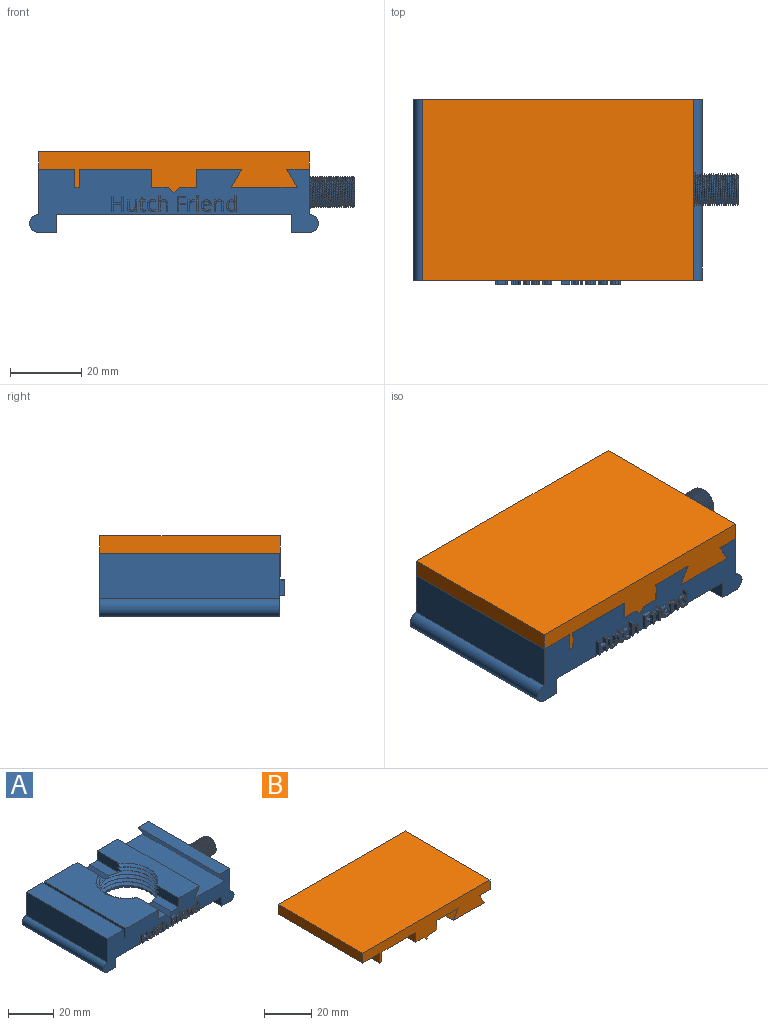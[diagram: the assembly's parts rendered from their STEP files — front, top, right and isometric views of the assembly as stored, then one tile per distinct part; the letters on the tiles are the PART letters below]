
ASSEMBLY  parts=2 mates=1
PART A: 264 faces, bbox 92x52.4x19.3 mm
  f0: cylinder r=12.7mm len=15.02mm, axis (0,0,-1), area 1.5mm2, adj f18,f23,f257,f259
  f1: cylinder r=12.7mm len=22mm, axis (0,0,-1), area 2.7mm2, adj f19,f22,f260,f262
  f2: cylinder r=12.7mm len=22mm, axis (0,0,-1), area 2.7mm2, adj f20,f23,f255,f258
  f3: cylinder r=12.7mm len=22mm, axis (0,0,-1), area 2.7mm2, adj f19,f22,f254,f261
  f4: cylinder r=12.7mm len=22mm, axis (0,0,-1), area 2.7mm2, adj f20,f23,f251,f256
  f5: cylinder r=12.7mm len=23.65mm, axis (0,0,-1), area 3.2mm2, adj f22,f43,f247,f253
  f6: cylinder r=12.7mm len=25.36mm, axis (0,0,-1), area 3.9mm2, adj f42,f45,f248,f252
  f7: plane 81.28x17.78mm, normal (0,-1,0), area 841.9mm2, adj f11,f12,f13,f14,f15,f16,f17,f18
  f8: cylinder r=12.7mm len=25.4mm, axis (0,0,-1), area 96.4mm2, adj f12,f44,f248,f249,f250
  f9: plane 81.28x17.78mm, normal (0,1,0), area 886.7mm2, adj f10,f12,f13,f14,f15,f16,f17,f18
  f10: plane 13.32x4.81mm, normal (0,0,1), area 59.4mm2, adj f9,f20,f42,f252
  f11: plane 13.21x4.83mm, normal (0,0,1), area 58.9mm2, adj f7,f23,f45,f251
  f12: plane 66.04x50.8mm, normal (0,0,-1), area 2848.1mm2, adj f7,f8,f9,f32,f34
  f13: plane 50.8x6.35mm, normal (0,0,1), area 322.6mm2, adj f7,f9,f16,f30
  f14: plane 51.12x20.64mm, normal (0,0,1), area 894.7mm2, adj f7,f9,f19,f22,f26,f262,f263
  f15: plane 50.8x10.16mm, normal (0,0,1), area 516.1mm2, adj f7,f9,f17,f25
  f16: plane 50.8x12.7mm, normal (1,0,0), area 510.6mm2, adj f7,f9,f13,f31,f36,f38,f40,f238
  f17: plane 50.8x12.7mm, normal (-1,0,0), area 645.2mm2, adj f7,f9,f15,f37
  f18: plane 51.04x12.94mm, normal (0,0,1), area 540.1mm2, adj f0,f7,f9,f20,f23,f28,f257,f259
  f19: plane 14.46x5.14mm, normal (1,0,0), area 68.2mm2, adj f1,f3,f9,f14,f21,f253,f254,f260
  f20: plane 14.46x5.14mm, normal (-1,0,0), area 68.2mm2, adj f2,f4,f9,f10,f18,f251,f252,f255
  f21: plane 14x4.87mm, normal (0,0,1), area 61.1mm2, adj f9,f19,f43,f253
  f22: plane 14.46x5.14mm, normal (1,0,0), area 69.1mm2, adj f1,f3,f5,f7,f14,f24,f247,f253
  f23: plane 14.46x5.14mm, normal (-1,0,0), area 69.1mm2, adj f0,f2,f4,f7,f11,f18,f251,f255
  f24: plane 13.86x4.85mm, normal (0,0,1), area 60.6mm2, adj f7,f22,f44,f247
  f25: plane 50.8x5.08mm, normal (1,0,0), area 258.1mm2, adj f7,f9,f15,f27
  f26: plane 50.8x5.08mm, normal (-1,0,0), area 258.1mm2, adj f7,f9,f14,f27
  f27: plane 50.8x1.27mm, normal (0,0,1), area 64.5mm2, adj f7,f9,f25,f26
  f28: plane 50.8x5.08mm, normal (0.87,0,-0.5), area 298mm2, adj f7,f9,f18,f29
  f29: plane 50.8x18.57mm, normal (0,0,1), area 943.1mm2, adj f7,f9,f28,f30
  f30: plane 50.8x5.08mm, normal (-0.87,0,-0.5), area 298mm2, adj f7,f9,f13,f29
  f31: cylinder r=4.76mm len=9.53mm, axis (-1,0,0), area 7.5mm2, adj f16,f236,f238
  f32: plane 50.8x5.08mm, normal (1,0,0), area 258.1mm2, adj f7,f9,f12,f33
  f33: plane 50.8x5.08mm, normal (0,0,-1), area 258.1mm2, adj f7,f9,f32,f37
  f34: plane 50.8x5.08mm, normal (-1,0,0), area 258.1mm2, adj f7,f9,f12,f35
  f35: plane 50.8x5.08mm, normal (0,0,-1), area 258.1mm2, adj f7,f9,f34,f36
  f36: cylinder r=2.54mm len=50.8mm, axis (0,-1,0), area 405.4mm2, adj f7,f9,f16,f35
  f37: cylinder r=2.54mm len=50.8mm, axis (0,-1,0), area 405.4mm2, adj f7,f9,f17,f33
  f38: cylinder r=3.17mm len=6.35mm, axis (1,0,0), area 50.7mm2, adj f16,f39
  f39: plane 6.35x6.35mm, normal (1,0,0), area 31.7mm2, adj f38
  f40: cylinder r=3.17mm len=6.35mm, axis (1,0,0), area 50.7mm2, adj f16,f41
  f41: plane 6.35x6.35mm, normal (1,0,0), area 31.7mm2, adj f40
  f42: plane 12.81x1.64mm, normal (-0.71,0,0.71), area 27mm2, adj f6,f9,f10,f43,f248,f249,f252
  f43: plane 12.82x1.65mm, normal (0.71,0,0.71), area 27mm2, adj f5,f9,f21,f42,f247,f249,f253
  f44: plane 12.75x1.63mm, normal (0.71,0,0.71), area 26.6mm2, adj f7,f8,f24,f45,f247,f248,f249
  f45: plane 12.75x1.64mm, normal (-0.71,0,0.71), area 26.6mm2, adj f6,f7,f11,f44,f248,f251,f252
  f46: plane 1.3x0.5mm, normal (0,0,-1), area 0.6mm2, adj f7,f47,f57,f58
  f47: plane 4.29x1.3mm, normal (1,0,0), area 5.6mm2, adj f7,f46,f48,f58
  f48: plane 1.3x0.5mm, normal (0,0,1), area 0.6mm2, adj f7,f47,f49,f58
  f49: plane 1.83x1.3mm, normal (-1,0,0), area 2.4mm2, adj f7,f48,f50,f58
  f50: plane 2.26x1.3mm, normal (0,0,1), area 2.9mm2, adj f7,f49,f51,f58
  f51: plane 1.83x1.3mm, normal (1,0,0), area 2.4mm2, adj f7,f50,f52,f58
  f52: plane 1.3x0.5mm, normal (0,0,1), area 0.6mm2, adj f7,f51,f53,f58
  f53: plane 4.29x1.3mm, normal (-1,0,0), area 5.6mm2, adj f7,f52,f54,f58
  f54: plane 1.3x0.5mm, normal (0,0,-1), area 0.6mm2, adj f7,f53,f55,f58
  f55: plane 2.02x1.3mm, normal (1,0,0), area 2.6mm2, adj f7,f54,f56,f58
  f56: plane 2.26x1.3mm, normal (0,0,-1), area 2.9mm2, adj f7,f55,f57,f58
  f57: plane 2.02x1.3mm, normal (-1,0,0), area 2.6mm2, adj f7,f46,f56,f58
  f58: plane 4.29x3.26mm, normal (0,-1,0), area 5.3mm2, adj f46,f47,f48,f49,f50,f51,f52,f53
  f59: plane 2.09x1.3mm, normal (1,0,0), area 2.7mm2, adj f7,f60,f75,f76
  f60: plane 1.3x0.49mm, normal (0,0,1), area 0.6mm2, adj f7,f59,f61,f76
  f61: plane 2.11x1.3mm, normal (-1,0,0), area 2.7mm2, adj f7,f60,f62,f76
  f62: extruded ~1.3x0.89mm, area 1.3mm2, adj f7,f61,f63,f76
  f63: extruded ~1.3x0.88mm, area 1.2mm2, adj f7,f62,f64,f76
  f64: extruded ~1.3x0.61mm, area 0.8mm2, adj f7,f63,f65,f76
  f65: extruded ~1.3x0.42mm, area 0.7mm2, adj f7,f64,f66,f76
  f66: plane 1.3x0.03mm, normal (0,0,-1), area 0mm2, adj f7,f65,f67,f76
  f67: plane 1.3x0.43mm, normal (-0.99,0,-0.16), area 0.6mm2, adj f7,f66,f68,f76
  f68: plane 1.3x0.4mm, normal (0,0,-1), area 0.5mm2, adj f7,f67,f69,f76
  f69: plane 3.22x1.3mm, normal (1,0,0), area 4.2mm2, adj f7,f68,f70,f76
  f70: plane 1.3x0.49mm, normal (0,0,1), area 0.6mm2, adj f7,f69,f71,f76
  f71: plane 1.69x1.3mm, normal (-1,0,0), area 2.2mm2, adj f7,f70,f72,f76
  f72: extruded ~1.3x0.9mm, area 1.2mm2, adj f7,f71,f73,f76
  f73: extruded ~1.3x0.74mm, area 1.1mm2, adj f7,f72,f74,f76
  f74: extruded ~1.3x0.56mm, area 0.8mm2, adj f7,f73,f75,f76
  f75: extruded ~1.3x0.59mm, area 0.8mm2, adj f7,f59,f74,f76
  f76: plane 3.28x2.69mm, normal (0,-1,0), area 3.8mm2, adj f59,f60,f61,f62,f63,f64,f65,f66
  f77: extruded ~1.3x0.25mm, area 0.3mm2, adj f7,f78,f95,f96
  f78: extruded ~1.3x0.38mm, area 0.5mm2, adj f7,f77,f79,f96
  f79: extruded ~1.3x0.45mm, area 0.6mm2, adj f7,f78,f80,f96
  f80: plane 1.89x1.3mm, normal (1,0,0), area 2.5mm2, adj f7,f79,f81,f96
  f81: plane 1.3x0.93mm, normal (0,0,-1), area 1.2mm2, adj f7,f80,f82,f96
  f82: plane 1.3x0.38mm, normal (1,0,0), area 0.5mm2, adj f7,f81,f83,f96
  f83: plane 1.3x0.93mm, normal (0,0,1), area 1.2mm2, adj f7,f82,f84,f96
  f84: plane 1.3x0.75mm, normal (1,0,0), area 1mm2, adj f7,f83,f85,f96
  f85: plane 1.3x0.28mm, normal (0,0,1), area 0.4mm2, adj f7,f84,f86,f96
  f86: plane 1.3x0.69mm, normal (-0.96,0,0.29), area 0.9mm2, adj f7,f85,f87,f96
  f87: plane 1.3x0.46mm, normal (-0.4,0,0.92), area 0.7mm2, adj f7,f86,f88,f96
  f88: plane 1.3x0.24mm, normal (-1,0,0), area 0.3mm2, adj f7,f87,f89,f96
  f89: plane 1.3x0.46mm, normal (0,0,-1), area 0.6mm2, adj f7,f88,f90,f96
  f90: plane 1.92x1.3mm, normal (-1,0,0), area 2.5mm2, adj f7,f89,f91,f96
  f91: extruded ~1.3x0.98mm, area 2mm2, adj f7,f90,f92,f96
  f92: extruded ~1.3x0.28mm, area 0.4mm2, adj f7,f91,f93,f96
  f93: extruded ~1.3x0.23mm, area 0.3mm2, adj f7,f92,f94,f96
  f94: plane 1.3x0.37mm, normal (1,0,0), area 0.5mm2, adj f7,f93,f95,f96
  f95: extruded ~1.3x0.19mm, area 0.3mm2, adj f7,f77,f94,f96
  f96: plane 4.02x1.91mm, normal (0,-1,0), area 2.7mm2, adj f77,f78,f79,f80,f81,f82,f83,f84
  f97: extruded ~1.3x1.08mm, area 1.6mm2, adj f7,f98,f111,f112
  f98: extruded ~1.3x0.81mm, area 1.1mm2, adj f7,f97,f99,f112
  f99: plane 1.3x0.43mm, normal (1,0,0), area 0.6mm2, adj f7,f98,f100,f112
  f100: extruded ~1.3x0.83mm, area 1.1mm2, adj f7,f99,f101,f112
  f101: extruded ~1.3x0.71mm, area 1mm2, adj f7,f100,f102,f112
  f102: extruded ~1.3x0.91mm, area 1.2mm2, adj f7,f101,f103,f112
  f103: extruded ~1.3x1.25mm, area 2.4mm2, adj f7,f102,f104,f112
  f104: extruded ~1.3x0.34mm, area 0.4mm2, adj f7,f103,f105,f112
  f105: extruded ~1.3x0.35mm, area 0.5mm2, adj f7,f104,f106,f112
  f106: plane 1.3x0.41mm, normal (0.94,0,-0.34), area 0.6mm2, adj f7,f105,f107,f112
  f107: extruded ~1.3x0.36mm, area 0.5mm2, adj f7,f106,f108,f112
  f108: extruded ~1.3x0.46mm, area 0.6mm2, adj f7,f107,f109,f112
  f109: extruded ~1.3x1.11mm, area 1.6mm2, adj f7,f108,f110,f112
  f110: extruded ~1.3x1.25mm, area 1.7mm2, adj f7,f109,f111,f112
  f111: extruded ~1.3x1.22mm, area 1.7mm2, adj f7,f97,f110,f112
  f112: plane 3.34x2.33mm, normal (0,-1,0), area 2.7mm2, adj f97,f98,f99,f100,f101,f102,f103,f104
  f113: plane 2.08x1.3mm, normal (-1,0,0), area 2.7mm2, adj f7,f114,f130,f131
  f114: plane 1.3x0.49mm, normal (0,0,-1), area 0.6mm2, adj f7,f113,f115,f131
  f115: plane 2.1x1.3mm, normal (1,0,0), area 2.7mm2, adj f7,f114,f116,f131
  f116: extruded ~1.3x0.89mm, area 1.3mm2, adj f7,f115,f117,f131
  f117: extruded ~1.3x0.89mm, area 1.2mm2, adj f7,f116,f118,f131
  f118: extruded ~1.3x0.61mm, area 0.8mm2, adj f7,f117,f119,f131
  f119: extruded ~1.3x0.41mm, area 0.7mm2, adj f7,f118,f120,f131
  f120: plane 1.3x0.03mm, normal (0,0,1), area 0mm2, adj f7,f119,f121,f131
  f121: extruded ~1.3x0.41mm, area 0.5mm2, adj f7,f120,f122,f131
  f122: plane 1.38x1.3mm, normal (1,0,0), area 1.8mm2, adj f7,f121,f123,f131
  f123: plane 1.3x0.49mm, normal (0,0,1), area 0.6mm2, adj f7,f122,f124,f131
  f124: plane 4.57x1.3mm, normal (-1,0,0), area 5.9mm2, adj f7,f123,f125,f131
  f125: plane 1.3x0.49mm, normal (0,0,-1), area 0.6mm2, adj f7,f124,f126,f131
  f126: plane 1.68x1.3mm, normal (1,0,0), area 2.2mm2, adj f7,f125,f127,f131
  f127: extruded ~1.3x0.9mm, area 1.2mm2, adj f7,f126,f128,f131
  f128: extruded ~1.3x0.74mm, area 1.1mm2, adj f7,f127,f129,f131
  f129: extruded ~1.3x0.56mm, area 0.8mm2, adj f7,f128,f130,f131
  f130: extruded ~1.3x0.59mm, area 0.8mm2, adj f7,f113,f129,f131
  f131: plane 4.57x2.69mm, normal (0,-1,0), area 4.4mm2, adj f113,f114,f115,f116,f117,f118,f119,f120
  f132: plane 1.3x0.5mm, normal (0,0,-1), area 0.6mm2, adj f7,f133,f141,f142
  f133: plane 1.84x1.3mm, normal (1,0,0), area 2.4mm2, adj f7,f132,f134,f142
  f134: plane 1.78x1.3mm, normal (0,0,-1), area 2.3mm2, adj f7,f133,f135,f142
  f135: plane 1.3x0.44mm, normal (1,0,0), area 0.6mm2, adj f7,f134,f136,f142
  f136: plane 1.78x1.3mm, normal (0,0,1), area 2.3mm2, adj f7,f135,f137,f142
  f137: plane 1.57x1.3mm, normal (1,0,0), area 2mm2, adj f7,f136,f138,f142
  f138: plane 1.89x1.3mm, normal (0,0,-1), area 2.5mm2, adj f7,f137,f139,f142
  f139: plane 1.3x0.44mm, normal (1,0,0), area 0.6mm2, adj f7,f138,f140,f142
  f140: plane 2.39x1.3mm, normal (0,0,1), area 3.1mm2, adj f7,f139,f141,f142
  f141: plane 4.29x1.3mm, normal (-1,0,0), area 5.6mm2, adj f7,f132,f140,f142
  f142: plane 4.29x2.39mm, normal (0,-1,0), area 3.8mm2, adj f132,f133,f134,f135,f136,f137,f138,f139
  f143: extruded ~1.3x0.38mm, area 0.5mm2, adj f7,f144,f155,f156
  f144: extruded ~1.3x0.56mm, area 0.8mm2, adj f7,f143,f145,f156
  f145: extruded ~1.3x0.48mm, area 0.9mm2, adj f7,f144,f146,f156
  f146: plane 1.3x0.02mm, normal (0,0,1), area 0mm2, adj f7,f145,f147,f156
  f147: plane 1.3x0.6mm, normal (1,0,0.09), area 0.8mm2, adj f7,f146,f148,f156
  f148: plane 1.3x0.4mm, normal (0,0,1), area 0.5mm2, adj f7,f147,f149,f156
  f149: plane 3.22x1.3mm, normal (-1,0,0), area 4.2mm2, adj f7,f148,f150,f156
  f150: plane 1.3x0.49mm, normal (0,0,-1), area 0.6mm2, adj f7,f149,f151,f156
  f151: plane 1.73x1.3mm, normal (1,0,0), area 2.2mm2, adj f7,f150,f152,f156
  f152: extruded ~1.3x0.79mm, area 1.1mm2, adj f7,f151,f153,f156
  f153: extruded ~1.3x0.67mm, area 1mm2, adj f7,f152,f154,f156
  f154: extruded ~1.3x0.35mm, area 0.5mm2, adj f7,f153,f155,f156
  f155: plane 1.3x0.45mm, normal (0.99,0,-0.15), area 0.6mm2, adj f7,f143,f154,f156
  f156: plane 3.28x1.85mm, normal (0,-1,0), area 2.2mm2, adj f143,f144,f145,f146,f147,f148,f149,f150
  f157: plane 1.3x0.49mm, normal (0,0,-1), area 0.6mm2, adj f7,f158,f160,f161
  f158: plane 3.22x1.3mm, normal (1,0,0), area 4.2mm2, adj f7,f157,f159,f161
  f159: plane 1.3x0.49mm, normal (0,0,1), area 0.6mm2, adj f7,f158,f160,f161
  f160: plane 3.22x1.3mm, normal (-1,0,0), area 4.2mm2, adj f7,f157,f159,f161
  f161: plane 3.22x0.49mm, normal (0,-1,0), area 1.6mm2, adj f157,f158,f159,f160
  f162: extruded ~1.3x0.25mm, area 0.3mm2, adj f7,f163,f169,f170
  f163: extruded ~1.3x0.25mm, area 0.3mm2, adj f7,f162,f164,f170
  f164: extruded ~1.3x0.21mm, area 0.3mm2, adj f7,f163,f165,f170
  f165: extruded ~1.3x0.2mm, area 0.3mm2, adj f7,f164,f166,f170
  f166: extruded ~1.3x0.25mm, area 0.3mm2, adj f7,f165,f167,f170
  f167: extruded ~1.3x0.24mm, area 0.3mm2, adj f7,f166,f168,f170
  f168: extruded ~1.3x0.2mm, area 0.3mm2, adj f7,f167,f169,f170
  f169: extruded ~1.3x0.21mm, area 0.3mm2, adj f7,f162,f168,f170
  f170: plane 0.65x0.58mm, normal (0,-1,0), area 0.3mm2, adj f162,f163,f164,f165,f166,f167,f168,f169
  f171: extruded ~1.3x0.62mm, area 0.9mm2, adj f172,f189,f190,f191
  f172: extruded ~1.3x0.59mm, area 0.9mm2, adj f171,f173,f190,f191
  f173: extruded ~1.3x0.71mm, area 1mm2, adj f172,f174,f190,f191
  f174: plane 1.68x1.3mm, normal (0,0,1), area 2.2mm2, adj f173,f189,f190,f191
  f175: extruded ~1.3x1.13mm, area 1.6mm2, adj f7,f176,f188,f190
  f176: extruded ~1.3x0.56mm, area 0.7mm2, adj f7,f175,f177,f190
  f177: extruded ~1.3x0.49mm, area 0.7mm2, adj f7,f176,f178,f190
  f178: plane 1.3x0.44mm, normal (1,0,0), area 0.6mm2, adj f7,f177,f179,f190
  f179: extruded ~1.3x1.03mm, area 1.4mm2, adj f7,f178,f180,f190
  f180: extruded ~1.3x0.77mm, area 1.1mm2, adj f7,f179,f181,f190
  f181: extruded ~1.3x0.86mm, area 1.2mm2, adj f7,f180,f182,f190
  f182: plane 2.22x1.3mm, normal (0,0,-1), area 2.9mm2, adj f7,f181,f183,f190
  f183: plane 1.3x0.31mm, normal (1,0,0), area 0.4mm2, adj f7,f182,f184,f190
  f184: extruded ~1.3x1.05mm, area 1.5mm2, adj f7,f183,f185,f190
  f185: extruded ~1.3x0.96mm, area 1.4mm2, adj f7,f184,f186,f190
  f186: extruded ~1.3x1.03mm, area 1.5mm2, adj f7,f185,f187,f190
  f187: extruded ~1.3x1.24mm, area 1.7mm2, adj f7,f186,f188,f190
  f188: extruded ~1.3x1.21mm, area 1.7mm2, adj f7,f175,f187,f190
  f189: extruded ~1.3x0.7mm, area 1mm2, adj f171,f174,f190,f191
  f190: plane 3.34x2.72mm, normal (0,-1,0), area 4.1mm2, adj f171,f172,f173,f174,f175,f176,f177,f178
  f191: plane 1.68x0.95mm, normal (0,-1,0), area 1.3mm2, adj f171,f172,f173,f174,f189
  f192: plane 2.08x1.3mm, normal (-1,0,0), area 2.7mm2, adj f7,f193,f208,f209
  f193: plane 1.3x0.49mm, normal (0,0,-1), area 0.6mm2, adj f7,f192,f194,f209
  f194: plane 2.1x1.3mm, normal (1,0,0), area 2.7mm2, adj f7,f193,f195,f209
  f195: extruded ~1.3x0.9mm, area 1.3mm2, adj f7,f194,f196,f209
  f196: extruded ~1.3x0.88mm, area 1.2mm2, adj f7,f195,f197,f209
  f197: extruded ~1.3x0.6mm, area 0.8mm2, adj f7,f196,f198,f209
  f198: extruded ~1.3x0.42mm, area 0.7mm2, adj f7,f197,f199,f209
  f199: plane 1.3x0.02mm, normal (0,0,1), area 0mm2, adj f7,f198,f200,f209
  f200: plane 1.3x0.44mm, normal (0.98,0,0.18), area 0.6mm2, adj f7,f199,f201,f209
  f201: plane 1.3x0.4mm, normal (0,0,1), area 0.5mm2, adj f7,f200,f202,f209
  f202: plane 3.22x1.3mm, normal (-1,0,0), area 4.2mm2, adj f7,f201,f203,f209
  f203: plane 1.3x0.49mm, normal (0,0,-1), area 0.6mm2, adj f7,f202,f204,f209
  f204: plane 1.69x1.3mm, normal (1,0,0), area 2.2mm2, adj f7,f203,f205,f209
  f205: extruded ~1.3x0.9mm, area 1.2mm2, adj f7,f204,f206,f209
  f206: extruded ~1.3x0.74mm, area 1.1mm2, adj f7,f205,f207,f209
  f207: extruded ~1.3x0.56mm, area 0.8mm2, adj f7,f206,f208,f209
  f208: extruded ~1.3x0.59mm, area 0.8mm2, adj f7,f192,f207,f209
  f209: plane 3.28x2.69mm, normal (0,-1,0), area 3.8mm2, adj f192,f193,f194,f195,f196,f197,f198,f199
  f210: extruded ~1.3x0.72mm, area 1mm2, adj f211,f233,f234,f235
  f211: extruded ~1.3x0.66mm, area 1mm2, adj f210,f212,f234,f235
  f212: extruded ~1.3x0.93mm, area 1.3mm2, adj f211,f213,f234,f235
  f213: extruded ~1.3x0.94mm, area 1.3mm2, adj f212,f214,f234,f235
  f214: extruded ~1.3x0.66mm, area 1mm2, adj f213,f215,f234,f235
  f215: extruded ~1.3x0.73mm, area 1.1mm2, adj f214,f216,f234,f235
  f216: extruded ~1.3x0.98mm, area 1.3mm2, adj f215,f217,f234,f235
  f217: plane 1.3x0.1mm, normal (-1,0,0), area 0.1mm2, adj f216,f233,f234,f235
  f218: plane 1.3x0.03mm, normal (0,0,-1), area 0mm2, adj f7,f219,f232,f234
  f219: plane 1.3x0.43mm, normal (-0.99,0,-0.15), area 0.6mm2, adj f7,f218,f220,f234
  f220: plane 1.3x0.4mm, normal (0,0,-1), area 0.5mm2, adj f7,f219,f221,f234
  f221: plane 4.57x1.3mm, normal (1,0,0), area 5.9mm2, adj f7,f220,f222,f234
  f222: plane 1.3x0.49mm, normal (0,0,1), area 0.6mm2, adj f7,f221,f223,f234
  f223: plane 1.31x1.3mm, normal (-1,0,0), area 1.7mm2, adj f7,f222,f224,f234
  f224: plane 1.3x0.23mm, normal (-1,0,-0.05), area 0.3mm2, adj f7,f223,f225,f234
  f225: plane 1.3x0.23mm, normal (-1,0,-0.09), area 0.3mm2, adj f7,f224,f226,f234
  f226: plane 1.3x0.04mm, normal (0,0,1), area 0.1mm2, adj f7,f225,f227,f234
  f227: extruded ~1.3x1mm, area 1.5mm2, adj f7,f226,f228,f234
  f228: extruded ~1.3x0.98mm, area 1.4mm2, adj f7,f227,f229,f234
  f229: extruded ~1.3x1.24mm, area 1.7mm2, adj f7,f228,f230,f234
  f230: extruded ~1.3x1.23mm, area 1.7mm2, adj f7,f229,f231,f234
  f231: extruded ~1.3x0.98mm, area 1.4mm2, adj f7,f230,f232,f234
  f232: extruded ~1.3x1.01mm, area 1.5mm2, adj f7,f218,f231,f234
  f233: extruded ~1.3x0.88mm, area 1.2mm2, adj f210,f217,f234,f235
  f234: plane 4.63x2.83mm, normal (0,-1,0), area 5mm2, adj f210,f211,f212,f213,f214,f215,f216,f217
  f235: plane 2.52x1.84mm, normal (0,-1,0), area 3.9mm2, adj f210,f211,f212,f213,f214,f215,f216,f217
  f236: plane 0.7x0.63mm, normal (0,-0.59,0.81), area 0.3mm2, adj f31,f237,f238,f239
  f237: bspline ~12.55x8.26mm, area 323.1mm2, adj f236,f238,f239,f245,f246
  f238: bspline ~9.52x9.51mm, area 11.5mm2, adj f16,f31,f236,f237
  f239: bspline ~12.58x10.2mm, area 316.2mm2, adj f236,f237,f245,f246
  f240: plane 5.08x5.08mm, normal (1,0,0), area 25.8mm2, adj f241,f242,f243,f244
  f241: plane 12.7x5.08mm, normal (0,1,0), area 64.5mm2, adj f240,f242,f244,f246
  f242: plane 12.7x5.08mm, normal (0,0,1), area 64.5mm2, adj f240,f241,f243,f246
  f243: plane 12.7x5.08mm, normal (0,-1,0), area 64.5mm2, adj f240,f242,f244,f246
  f244: plane 12.7x5.08mm, normal (0,0,-1), area 64.5mm2, adj f240,f241,f243,f246
  f245: cone r=4.06mm half-angle=45deg, axis (-1,0,0), area 5.4mm2, adj f237,f239,f246
  f246: plane 8.16x8.16mm, normal (1,0,0), area 25.9mm2, adj f237,f239,f241,f242,f243,f244,f245
  f247: bspline ~33.13x21.52mm, area 72.9mm2, adj f5,f22,f24,f43,f44,f249
  f248: bspline ~33.13x28.69mm, area 418.7mm2, adj f6,f8,f42,f44,f45,f249,f250
  f249: bspline ~33.13x28.69mm, area 499.6mm2, adj f8,f42,f43,f44,f247,f248,f250
  f250: plane 1.9x1.34mm, normal (0.81,-0.59,0), area 1.6mm2, adj f8,f248,f249
  f251: bspline ~33.13x21.52mm, area 59.5mm2, adj f4,f11,f20,f23,f45,f252
  f252: bspline ~33.13x21.52mm, area 72.4mm2, adj f6,f10,f20,f42,f45,f251
  f253: bspline ~33.13x21.52mm, area 58.9mm2, adj f5,f19,f21,f22,f43,f254
  f254: bspline ~33.13x21.52mm, area 55.5mm2, adj f3,f19,f22,f253
  f255: bspline ~33.13x21.52mm, area 55.5mm2, adj f2,f20,f23,f256
  f256: bspline ~33.13x21.52mm, area 55.5mm2, adj f4,f20,f23,f255
  f257: bspline ~33.13x21.52mm, area 53.4mm2, adj f0,f18,f20,f23,f258
  f258: bspline ~33.13x21.52mm, area 55.5mm2, adj f2,f20,f23,f257
  f259: bspline ~21.52x16.56mm, area 4.6mm2, adj f0,f18,f23
  f260: bspline ~33.13x21.52mm, area 55.5mm2, adj f1,f19,f22,f261
  f261: bspline ~33.13x21.52mm, area 55.5mm2, adj f3,f19,f22,f260
  f262: bspline ~33.13x21.52mm, area 51.6mm2, adj f1,f14,f19,f22,f263
  f263: bspline ~28.99x21.52mm, area 7.1mm2, adj f14,f19,f262
PART B: 46 faces, bbox 76.3x50.9x12.4 mm
  f0: cylinder r=12.7mm len=12.7mm, axis (0,0,-1), area 1.3mm2, adj f10,f12,f38,f41
  f1: cylinder r=12.7mm len=1.2mm, axis (0,0,-1), area 0.1mm2, adj f6,f27,f34,f36
  f2: cylinder r=12.7mm len=7.91mm, axis (0,0,-1), area 0.8mm2, adj f7,f8,f10,f26,f37,f40,f45
  f3: cylinder r=12.7mm len=12.7mm, axis (0,0,-1), area 1.3mm2, adj f9,f11,f33,f43
  f4: cylinder r=12.7mm len=25.4mm, axis (0,0,-1), area 310.3mm2, adj f9,f10,f11,f12,f13,f14,f32,f42
  f5: plane 14.1x4.76mm, normal (0,0,-1), area 63.1mm2, adj f12,f21,f26,f37
  f6: plane 12.76x1.64mm, normal (-0.71,0,-0.71), area 27.1mm2, adj f1,f20,f25,f27,f33,f34,f36
  f7: plane 12.86x1.65mm, normal (0.71,0,-0.71), area 26.5mm2, adj f2,f8,f21,f26,f39,f40
  f8: plane 14.28x4.8mm, normal (0,0,-1), area 63.7mm2, adj f2,f7,f10,f21,f45
  f9: plane 14.46x5.14mm, normal (1,0,0), area 70.8mm2, adj f3,f4,f13,f20,f28,f33,f43,f44
  f10: plane 14.46x5.14mm, normal (1,0,0), area 69.6mm2, adj f0,f2,f4,f8,f13,f21,f37,f38
  f11: plane 14.46x5.14mm, normal (-1,0,0), area 70.3mm2, adj f3,f4,f14,f20,f25,f33,f35,f43
  f12: plane 14.46x5.14mm, normal (-1,0,0), area 69.6mm2, adj f0,f4,f5,f14,f21,f37,f38,f41
  f13: plane 50.8x12.7mm, normal (0,0,-1), area 546.1mm2, adj f4,f9,f10,f20,f21,f29
  f14: plane 50.8x20.32mm, normal (0,0,-1), area 933.2mm2, adj f4,f11,f12,f20,f21,f24
  f15: plane 50.8x10.16mm, normal (0,0,-1), area 516.1mm2, adj f17,f20,f21,f22
  f16: plane 76.2x50.8mm, normal (0,0,1), area 3871mm2, adj f17,f19,f20,f21
  f17: plane 50.8x5mm, normal (-1,0,0), area 254mm2, adj f15,f16,f20,f21
  f18: plane 50.8x6.35mm, normal (0,0,-1), area 322.6mm2, adj f19,f20,f21,f31
  f19: plane 50.8x5mm, normal (1,0,0), area 254mm2, adj f16,f18,f20,f21
  f20: plane 76.2x11.67mm, normal (0,1,0), area 533.9mm2, adj f6,f9,f11,f13,f14,f15,f16,f17
  f21: plane 76.2x11.67mm, normal (0,-1,0), area 533.9mm2, adj f5,f7,f8,f10,f12,f13,f14,f15
  f22: plane 50.8x5.08mm, normal (-1,0,0), area 258.1mm2, adj f15,f20,f21,f23
  f23: plane 50.8x1.27mm, normal (0,0,-1), area 64.5mm2, adj f20,f21,f22,f24
  f24: plane 50.8x5.08mm, normal (1,0,0), area 258.1mm2, adj f14,f20,f21,f23
  f25: plane 12.83x4.84mm, normal (0,0,-1), area 56.2mm2, adj f6,f11,f20,f33,f35
  f26: plane 12.86x1.65mm, normal (-0.71,0,-0.71), area 26.6mm2, adj f2,f5,f7,f21,f37,f39,f40
  f27: plane 12.76x1.63mm, normal (0.71,0,-0.71), area 27mm2, adj f1,f6,f20,f28,f33,f34,f36
  f28: plane 12.9x4.76mm, normal (0,0,-1), area 56.8mm2, adj f9,f20,f27,f33
  f29: plane 50.8x5.08mm, normal (-0.87,0,0.5), area 298mm2, adj f13,f20,f21,f30
  f30: plane 50.8x18.57mm, normal (0,0,-1), area 943.1mm2, adj f20,f21,f29,f31
  f31: plane 50.8x5.08mm, normal (0.87,0,0.5), area 298mm2, adj f18,f20,f21,f30
  f32: plane 25.4x25.4mm, normal (0,0,-1), area 506.7mm2, adj f4
  f33: bspline ~21.52x16.56mm, area 23.8mm2, adj f3,f6,f9,f11,f25,f27,f28,f34
  f34: bspline ~14.35x5.57mm, area 4mm2, adj f1,f6,f27,f33
  f35: bspline ~14.35x5.57mm, area 0.5mm2, adj f11,f25,f33
  f36: bspline ~14.35x5.57mm, area 0.5mm2, adj f1,f6,f27
  f37: bspline ~21.52x16.56mm, area 24.3mm2, adj f2,f5,f10,f12,f26,f38
  f38: bspline ~28.69x16.56mm, area 25.2mm2, adj f0,f10,f12,f37
  f39: bspline ~14.35x5.57mm, area 0.6mm2, adj f7,f26,f40
  f40: bspline ~14.35x5.57mm, area 4mm2, adj f2,f7,f26,f39
  f41: bspline ~14.35x3.35mm, area 25.2mm2, adj f0,f10,f12,f42
  f42: bspline ~21.52x16.56mm, area 25.2mm2, adj f4,f10,f12,f41
  f43: bspline ~21.52x16.56mm, area 25.2mm2, adj f3,f9,f11,f44
  f44: bspline ~21.52x16.56mm, area 25.2mm2, adj f4,f9,f11,f43
  f45: bspline ~14.35x5.57mm, area 0.3mm2, adj f2,f8,f10
PLACE A t=(14.29,23.33,-17.69)mm
PLACE B t=(14.29,-2.19,0.01)mm
MATE slider B.f21 <-> A.f7  axis (0,-1,0) through (-23.81,-2.19,-4.99)mm
